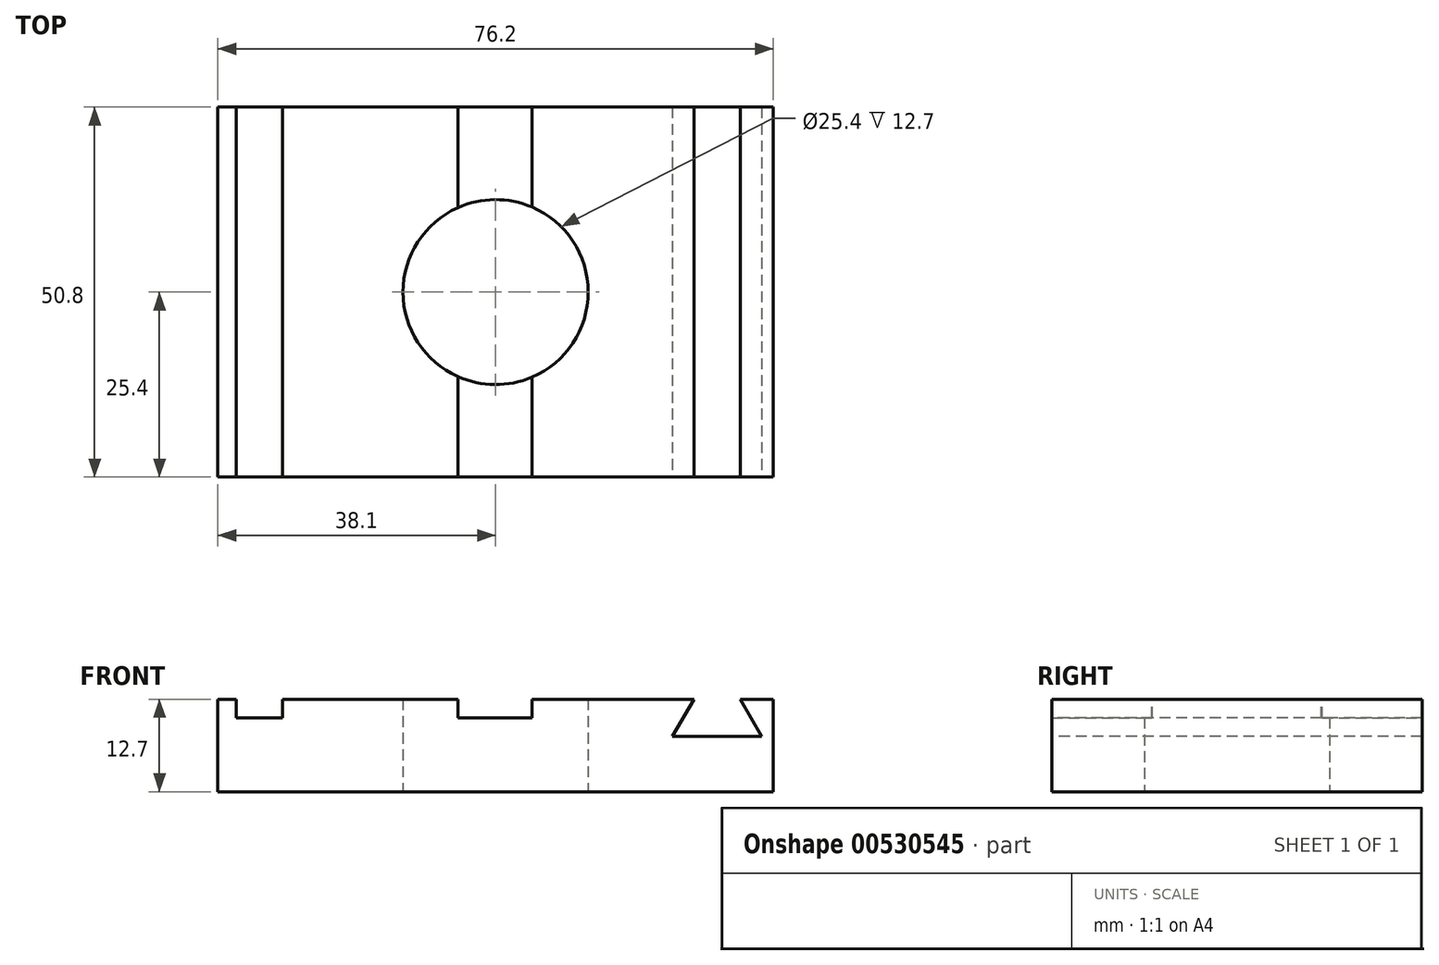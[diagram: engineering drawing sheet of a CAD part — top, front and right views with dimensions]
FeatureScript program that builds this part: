
annotation { "Feature Type Name" : "Feature", "Feature Type Description" : "" }
export const myFeature = defineFeature(function(context is Context, id is Id, definition is map)
    precondition{}
    {
        {
            var Q0;
            Q0=qCreatedBy(makeId("Top.planeOp"),FACE);
            var sketch = newSketch(context, id + "F0", { "sketchPlane" : qUnion([Q0])});
            skLineSegment(sketch, "E0.bottom", {"start": v(-38.1, 25.4) * mm, "end": v(38.1, 25.4) * mm});
            skLineSegment(sketch, "E0.top", {"start": v(-38.1, -25.4) * mm, "end": v(38.1, -25.4) * mm});
            skLineSegment(sketch, "E0.left", {"start": v(-38.1, 25.4) * mm, "end": v(-38.1, -25.4) * mm});
            skLineSegment(sketch, "E0.right", {"start": v(38.1, 25.4) * mm, "end": v(38.1, -25.4) * mm});
            skPoint(sketch, "E0.middle", {"position": v(0, 0) * mm});
            skCircle(sketch, "E1", {"center": v(0, 0) * mm, "radius": 12.7 * mm});
            skSolve(sketch);
        }
        {
            var Q0;
            Q0 = qSketchRegion(id + "F0", true);
            extrude(context, id + "F1", {"entities" : qUnion([Q0]), "depth" : 12.7 * mm, "offsetDistance" : 25.4 * mm});
        }
        {
            var Q0;
            Q0=makeQuery(id+"F1.opExtrude","CAP_FACE",FACE,{"disambiguationData":[OSD([sQuery(id+"F0.wireOp",EDGE,"E0.bottom"),sQuery(id+"F0.wireOp",EDGE,"E0.top"),sQuery(id+"F0.wireOp",EDGE,"E0.left"),sQuery(id+"F0.wireOp",EDGE,"E0.right"),sQuery(id+"F0.wireOp",EDGE,"E1")])],"isStart":false});
            var sketch = newSketch(context, id + "F2", { "sketchPlane" : qUnion([Q0])});
            skLineSegment(sketch, "E2.bottom", {"start": v(-35.56, 25.4) * mm, "end": v(-29.2, 25.4) * mm});
            skLineSegment(sketch, "E2.top", {"start": v(-35.56, -25.4) * mm, "end": v(-29.2, -25.4) * mm});
            skLineSegment(sketch, "E2.left", {"start": v(-35.56, 25.4) * mm, "end": v(-35.56, -25.4) * mm});
            skLineSegment(sketch, "E2.right", {"start": v(-29.2, 25.4) * mm, "end": v(-29.2, -25.4) * mm});
            skLineSegment(sketch, "E3", {"start": v(-5.19, 25.4) * mm, "end": v(-5.19, -25.4) * mm});
            skLineSegment(sketch, "E4", {"start": v(-5.19, -25.4) * mm, "end": v(4.97, -25.4) * mm});
            skLineSegment(sketch, "E5", {"start": v(4.97, -25.4) * mm, "end": v(4.97, 25.4) * mm});
            skLineSegment(sketch, "E6", {"start": v(4.97, 25.4) * mm, "end": v(-5.19, 25.4) * mm});
            skPoint(sketch, "E7", {"position": v(0, 0) * mm});
            skPoint(sketch, "E8", {"position": v(-0.1, 25.4) * mm});
            skPoint(sketch, "E9", {"position": v(0, -25.4) * mm});
            skLineSegment(sketch, "E10", {"start": v(-0.1, 25.4) * mm, "end": v(0, -25.4) * mm, "construction": true});
            skSolve(sketch);
        }
        {
            var Q0;
            {var subQ0=sQuery(id+"F2.wireOp",EDGE,"E4");Q0=makeQuery(id+"F2.imprint","IMPRINT",FACE,{"disambiguationData":[TD([[makeQuery(id+"F2.imprint","IMPRINT",EDGE,{"derivedFrom":subQ0}),1.0]])]});}
            var Q1;
            {var subQ0=sQuery(id+"F2.wireOp",EDGE,"E6");Q1=makeQuery(id+"F2.imprint","IMPRINT",FACE,{"disambiguationData":[TD([[makeQuery(id+"F2.imprint","IMPRINT",EDGE,{"derivedFrom":subQ0}),-1.0]])]});}
            var Q2;
            Q2=makeQuery(id+"F2.imprint","IMPRINT",FACE,{"disambiguationData":[TD([[makeQuery(id+"F2.imprint","IMPRINT",EDGE,{"derivedFrom":sQuery(id+"F2.wireOp",EDGE,"E2.bottom")}),-1.0]])]});
            extrude(context, id + "F3", {"entities" : qUnion([Q0, Q1, Q2]), "operationType" : NewBodyOperationType.REMOVE, "oppositeDirection" : true, "depth" : 2.54 * mm, "offsetDistance" : 25.4 * mm});
        }
        {
            var Q0;
            Q0=makeQuery(id+"F1.opExtrude","SWEPT_FACE",FACE,{"disambiguationData":[OSD([sQuery(id+"F0.wireOp",EDGE,"E0.top")])]});
            var sketch = newSketch(context, id + "F4", { "sketchPlane" : qUnion([Q0])});
            skLineSegment(sketch, "E11", {"start": v(27.2, 12.7) * mm, "end": v(24.27, 7.62) * mm});
            skLineSegment(sketch, "E12", {"start": v(24.27, 7.62) * mm, "end": v(36.48, 7.62) * mm});
            skLineSegment(sketch, "E13", {"start": v(36.48, 7.62) * mm, "end": v(33.55, 12.7) * mm});
            skLineSegment(sketch, "E14", {"start": v(33.55, 12.7) * mm, "end": v(27.2, 12.7) * mm});
            skLineSegment(sketch, "E15", {"start": v(30.37, 7.62) * mm, "end": v(30.37, 12.7) * mm, "construction": true});
            skSolve(sketch);
        }
        {
            var Q0;
            Q0=makeQuery(id+"F4.imprint","IMPRINT",FACE,{"disambiguationData":[TD([[makeQuery(id+"F4.imprint","IMPRINT",EDGE,{"derivedFrom":sQuery(id+"F4.wireOp",EDGE,"E11")}),1.0]])]});
            extrude(context, id + "F5", {"entities" : qUnion([Q0]), "operationType" : NewBodyOperationType.REMOVE, "endBound" : BoundingType.UP_TO_NEXT, "oppositeDirection" : true, "depth" : 50.8 * mm, "offsetDistance" : 25.4 * mm});
        }
    });
